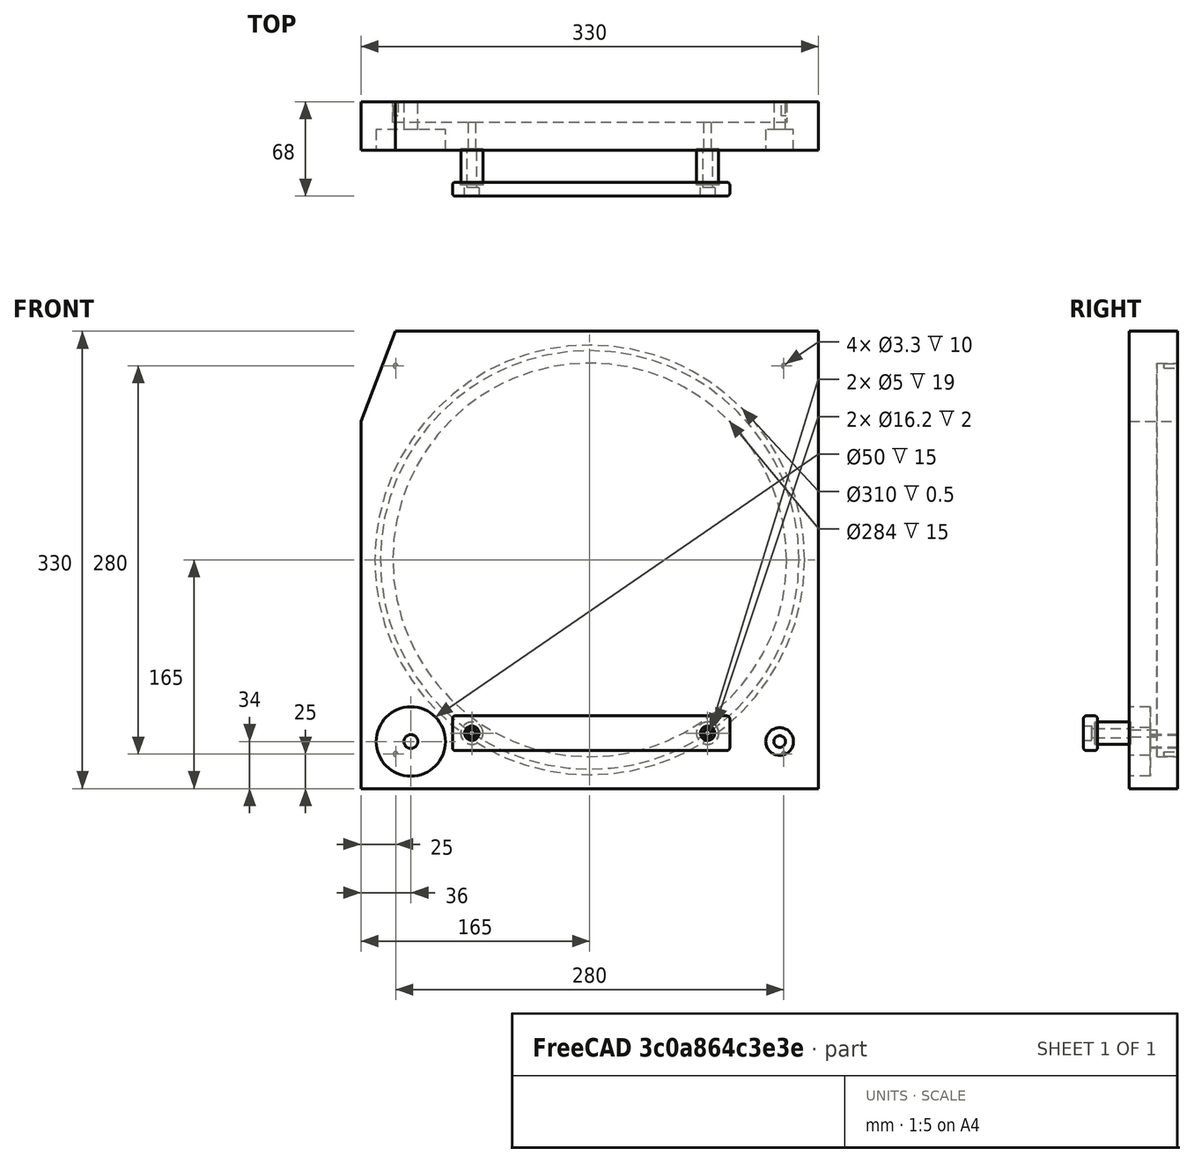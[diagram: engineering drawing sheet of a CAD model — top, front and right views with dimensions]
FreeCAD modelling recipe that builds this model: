
FCSTD DOCUMENT  (FreeCAD 0.20R29603 (Git))
Label: XL30SimpleFrontdoor01
License: All rights reserved
LicenseURL: http://en.wikipedia.org/wiki/All_rights_reserved
objects: Part::Cylinder×25, Part::Cut×13, Part::MultiFuse×7, Part::Box×3, Part::Feature×3, Part::Fillet×1
note: 52 computed .brp shape members not serialized (recipe doc carries the construction recipe); baked Part::Feature solids carry a one-line shape summary decoded from their .brp

FEATURE [Part::Box] Box  label="Würfel"
  AttacherType = Attacher::AttachEngine3D
  Height = 330
  Length = 330
  Width = 35
FEATURE [Part::Box] Box001  label="Würfel001"
  AttacherType = Attacher::AttachEngine3D
  Height = 50
  Length = 70
  Placement = pos=(0,0,265) rot=(0,-1,0;1.20428rad)
  Width = 35
FEATURE [Part::Cut] Cut
  Base = -> Box
  Tool = -> Box001
FEATURE [Part::Cylinder] Cylinder  label="Zylinder"
  Angle = 360
  AttacherType = Attacher::AttachEngine3D
  FirstAngle = 0
  Height = 40
  Placement = pos=(302,0,34) rot=(1,0,0;-1.5708rad)
  Radius = 4.2
  SecondAngle = 0
FEATURE [Part::Cylinder] Cylinder001  label="Zylinder001"
  Angle = 360
  AttacherType = Attacher::AttachEngine3D
  FirstAngle = 0
  Height = 40
  Placement = pos=(36,0,34) rot=(-1,0,0;1.5708rad)
  Radius = 5
  SecondAngle = 0
FEATURE [Part::Cylinder] Cylinder002  label="Zylinder002"
  Angle = 360
  AttacherType = Attacher::AttachEngine3D
  FirstAngle = 0
  Height = 15
  Placement = pos=(302,0,34) rot=(-1,0,0;1.5708rad)
  Radius = 10
  SecondAngle = 0
FEATURE [Part::Cylinder] Cylinder003  label="Zylinder003"
  Angle = 360
  AttacherType = Attacher::AttachEngine3D
  FirstAngle = 0
  Height = 15
  Placement = pos=(36,0,34) rot=(-1,0,0;1.5708rad)
  Radius = 25
  SecondAngle = 0
FEATURE [Part::MultiFuse] Fusion
  Shapes = -> [Cylinder002,Cylinder]
FEATURE [Part::MultiFuse] Fusion001
  Shapes = -> [Cylinder001,Cylinder003]
FEATURE [Part::MultiFuse] Fusion002
  Shapes = -> [Fusion,Fusion001]
FEATURE [Part::Cut] Cut001
  Base = -> Cut
  Tool = -> Fusion002
FEATURE [Part::Cylinder] Cylinder004  label="Zylinder004"
  Angle = 360
  AttacherType = Attacher::AttachEngine3D
  FirstAngle = 0
  Height = 0.5
  Radius = 155
  SecondAngle = 0
FEATURE [Part::Cylinder] Cylinder005  label="Zylinder005"
  Angle = 360
  AttacherType = Attacher::AttachEngine3D
  FirstAngle = 0
  Height = 0.5
  Radius = 151
  SecondAngle = 0
FEATURE [Part::Cut] Cut002
  Base = -> Cylinder004
  Placement = pos=(165,35,165) rot=(1,0,0;1.5708rad)
  Tool = -> Cylinder005
FEATURE [Part::Cut] Cut003
  Base = -> Cut001
  Tool = -> Cut002
FEATURE [Part::Cylinder] Cylinder006  label="Zylinder006"
  Angle = 360
  AttacherType = Attacher::AttachEngine3D
  FirstAngle = 0
  Height = 180
  Placement = pos=(165,200,165) rot=(1,0,0;1.5708rad)
  Radius = 142
  SecondAngle = 0
FEATURE [Part::Cut] Cut004
  Base = -> Cut003
  Tool = -> Cylinder006
FEATURE [Part::Cylinder] Cylinder007  label="Zylinder007"
  Angle = 360
  AttacherType = Attacher::AttachEngine3D
  FirstAngle = 0
  Height = 20
  Placement = pos=(80,20,40) rot=(1,0,0;1.5708rad)
  Radius = 2.5
  SecondAngle = 0
FEATURE [Part::Cylinder] Cylinder008  label="Zylinder008"
  Angle = 360
  AttacherType = Attacher::AttachEngine3D
  FirstAngle = 0
  Height = 20
  Placement = pos=(250,20,40) rot=(1,0,0;1.5708rad)
  Radius = 2.5
  SecondAngle = 0
FEATURE [Part::MultiFuse] Fusion003
  Shapes = -> [Cylinder007,Cylinder008]
FEATURE [Part::Cut] Cut005
  Base = -> Cut004
  Tool = -> Fusion003
FEATURE [Part::Cylinder] Cylinder009  label="Zylinder009"
  Angle = 360
  AttacherType = Attacher::AttachEngine3D
  FirstAngle = 0
  Height = 25
  Placement = pos=(80,0,40) rot=(1,0,0;1.5708rad)
  Radius = 8
  SecondAngle = 0
FEATURE [Part::Cylinder] Cylinder010  label="Zylinder010"
  Angle = 360
  AttacherType = Attacher::AttachEngine3D
  FirstAngle = 0
  Height = 25
  Placement = pos=(250,0,40) rot=(1,0,0;1.5708rad)
  Radius = 8
  SecondAngle = 0
FEATURE [Part::Cylinder] Cylinder011  label="Zylinder011"
  Angle = 360
  AttacherType = Attacher::AttachEngine3D
  FirstAngle = 0
  Height = 25
  Placement = pos=(80,0,40) rot=(1,0,0;1.5708rad)
  Radius = 3.3
  SecondAngle = 0
FEATURE [Part::Cylinder] Cylinder012  label="Zylinder012"
  Angle = 360
  AttacherType = Attacher::AttachEngine3D
  FirstAngle = 0
  Height = 25
  Placement = pos=(250,0,40) rot=(1,0,0;1.5708rad)
  Radius = 3.3
  SecondAngle = 0
FEATURE [Part::Cut] Cut006  label="Spacer01"
  Base = -> Cylinder009
  Tool = -> Cylinder011
FEATURE [Part::Cut] Cut007  label="Spacer02"
  Base = -> Cylinder010
  Tool = -> Cylinder012
FEATURE [Part::Box] Box002  label="Würfel002"
  AttacherType = Attacher::AttachEngine3D
  Height = 25
  Length = 200
  Placement = pos=(66,-28,27.5) rot=(0,0,1;0rad)
  Width = 10
FEATURE [Part::Cylinder] Cylinder013  label="Zylinder013"
  Angle = 360
  AttacherType = Attacher::AttachEngine3D
  FirstAngle = 0
  Height = 20
  Placement = pos=(80,0,40) rot=(1,0,0;1.5708rad)
  Radius = 8.1
  SecondAngle = 0
FEATURE [Part::Cylinder] Cylinder014  label="Zylinder014"
  Angle = 360
  AttacherType = Attacher::AttachEngine3D
  FirstAngle = 0
  Height = 20
  Placement = pos=(250,0,40) rot=(1,0,0;1.5708rad)
  Radius = 8.1
  SecondAngle = 0
FEATURE [Part::Cut] Cut008
  Base = -> Box002
  Tool = -> Cylinder013
FEATURE [Part::Cut] Cut009
  Base = -> Cut008
  Tool = -> Cylinder014
FEATURE [Part::Cylinder] Cylinder015  label="Zylinder015"
  Angle = 360
  AttacherType = Attacher::AttachEngine3D
  FirstAngle = 0
  Height = 6
  Placement = pos=(80,-22,40) rot=(1,0,0;1.5708rad)
  Radius = 5.2
  SecondAngle = 0
FEATURE [Part::Cylinder] Cylinder016  label="Zylinder016"
  Angle = 360
  AttacherType = Attacher::AttachEngine3D
  FirstAngle = 0
  Height = 6
  Placement = pos=(250,-22,40) rot=(1,0,0;1.5708rad)
  Radius = 5.2
  SecondAngle = 0
FEATURE [Part::Cylinder] Cylinder017  label="Zylinder017"
  Angle = 360
  AttacherType = Attacher::AttachEngine3D
  FirstAngle = 0
  Height = 20
  Placement = pos=(80,-10,40) rot=(1,0,0;1.5708rad)
  Radius = 3.3
  SecondAngle = 0
FEATURE [Part::Cylinder] Cylinder018  label="Zylinder018"
  Angle = 360
  AttacherType = Attacher::AttachEngine3D
  FirstAngle = 0
  Height = 20
  Placement = pos=(250,-10,40) rot=(1,0,0;1.5708rad)
  Radius = 3.3
  SecondAngle = 0
FEATURE [Part::MultiFuse] Fusion004
  Shapes = -> [Cylinder015,Cylinder016,Cylinder017,Cylinder018]
FEATURE [Part::Cut] Cut010  label="HandleWithoutPhases"
  Base = -> Cut009
  Tool = -> Fusion004
FEATURE [Part::Fillet] Fillet  label="HandleWithFillet"
  Base = -> Cut010
  Edges = 12 edges r=2: [Edge1,Edge2,Edge3,Edge4,Edge5,Edge6,Edge7,Edge10,Edge11,Edge12,Edge13,Edge16]
  Placement = pos=(0,-5,0) rot=(0,0,1;0rad)
FEATURE [Part::Cylinder] Cylinder019  label="Zylinder019"
  Angle = 360
  AttacherType = Attacher::AttachEngine3D
  FirstAngle = 0
  Height = 20
  Placement = pos=(250,1,40) rot=(1,0,0;1.5708rad)
  Radius = 8.1
  SecondAngle = 0
FEATURE [Part::Cylinder] Cylinder020  label="Zylinder020"
  Angle = 360
  AttacherType = Attacher::AttachEngine3D
  FirstAngle = 0
  Height = 20
  Placement = pos=(80,1,40) rot=(1,0,0;1.5708rad)
  Radius = 8.1
  SecondAngle = 0
FEATURE [Part::MultiFuse] Fusion005
  Shapes = -> [Cylinder019,Cylinder020]
FEATURE [Part::Cut] Cut011
  Base = -> Cut005
  Tool = -> Fusion005
FEATURE [Part::Cylinder] Cylinder021  label="Zylinder021"
  Angle = 360
  AttacherType = Attacher::AttachEngine3D
  FirstAngle = 0
  Height = 10
  Placement = pos=(25,35,25) rot=(1,0,0;1.5708rad)
  Radius = 1.65
  SecondAngle = 0
FEATURE [Part::Cylinder] Cylinder022  label="Zylinder022"
  Angle = 360
  AttacherType = Attacher::AttachEngine3D
  FirstAngle = 0
  Height = 10
  Placement = pos=(305,35,25) rot=(1,0,0;1.5708rad)
  Radius = 1.65
  SecondAngle = 0
FEATURE [Part::Cylinder] Cylinder023  label="Zylinder023"
  Angle = 360
  AttacherType = Attacher::AttachEngine3D
  FirstAngle = 0
  Height = 10
  Placement = pos=(25,35,305) rot=(1,0,0;1.5708rad)
  Radius = 1.65
  SecondAngle = 0
FEATURE [Part::Cylinder] Cylinder024  label="Zylinder024"
  Angle = 360
  AttacherType = Attacher::AttachEngine3D
  FirstAngle = 0
  Height = 10
  Placement = pos=(305,35,305) rot=(1,0,0;1.5708rad)
  Radius = 1.65
  SecondAngle = 0
FEATURE [Part::MultiFuse] Fusion006  label="HoleForM4CopperScrew"
  Shapes = -> [Cylinder024,Cylinder021,Cylinder022,Cylinder023]
FEATURE [Part::Cut] Cut012  label="SimpleFrontdoor01"
  Base = -> Cut011
  Tool = -> Fusion006
FEATURE [Part::Feature] Cut006_solid  label="XL30SimpleFrontdoor01_HandleSpacer"
  shape: bbox 16 x 25 x 16 mm, 4 faces (baked)
FEATURE [Part::Feature] Fillet_solid  label="XL30SimpleFrontdoor01_Handle"
  shape: bbox 200 x 10 x 25 mm, 36 faces (baked)
FEATURE [Part::Feature] Cut012_solid  label="XL30SimpleFrontdoor01"
  shape: bbox 330 x 35 x 330 mm, 35 faces (baked)
